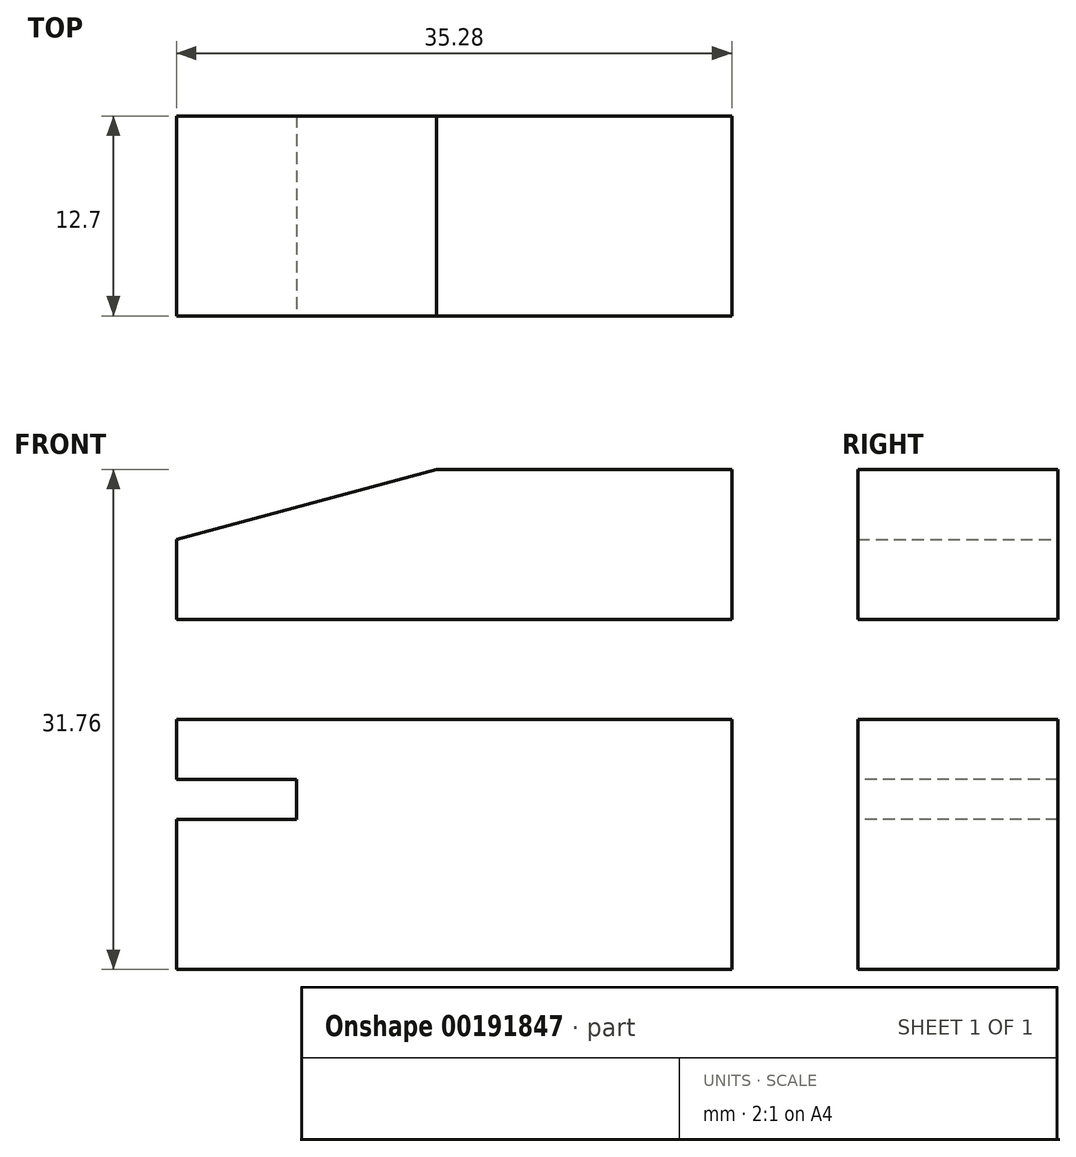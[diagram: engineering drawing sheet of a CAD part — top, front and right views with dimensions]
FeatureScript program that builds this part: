
annotation { "Feature Type Name" : "Feature", "Feature Type Description" : "" }
export const myFeature = defineFeature(function(context is Context, id is Id, definition is map)
    precondition{}
    {
        {
            var Q0;
            Q0=qCreatedBy(makeId("Front.planeOp"),FACE);
            var sketch = newSketch(context, id + "F0", { "sketchPlane" : qUnion([Q0])});
            skLineSegment(sketch, "E0.bottom", {"start": v(0, 0) * mm, "end": v(18.75, 0) * mm});
            skLineSegment(sketch, "E0.top", {"start": v(0, 9.52) * mm, "end": v(18.75, 9.52) * mm});
            skLineSegment(sketch, "E0.left", {"start": v(0, 0) * mm, "end": v(0, 9.52) * mm, "construction": true});
            skLineSegment(sketch, "E0.right", {"start": v(18.75, 0) * mm, "end": v(18.75, 9.52) * mm});
            skLineSegment(sketch, "E1", {"start": v(0, 9.52) * mm, "end": v(-16.53, 5.1) * mm});
            skLineSegment(sketch, "E2", {"start": v(-16.53, 5.1) * mm, "end": v(-16.53, 0) * mm});
            skLineSegment(sketch, "E3", {"start": v(-16.53, 0) * mm, "end": v(0, 0) * mm});
            skSolve(sketch);
        }
        {
            var Q0;
            Q0=makeQuery(id+"F0.imprint","IMPRINT",FACE,{"disambiguationData":[TD([[makeQuery(id+"F0.imprint","IMPRINT",EDGE,{"derivedFrom":sQuery(id+"F0.wireOp",EDGE,"E0.bottom")}),1.0]])]});
            extrude(context, id + "F1", {"entities" : qUnion([Q0]), "endBound" : BoundingType.SYMMETRIC, "depth" : 12.7 * mm});
        }
        {
            var Q0;
            Q0=qCreatedBy(makeId("Front.planeOp"),FACE);
            var sketch = newSketch(context, id + "F2", { "sketchPlane" : qUnion([Q0])});
            skLineSegment(sketch, "E4.bottom", {"start": v(18.75, -12.7) * mm, "end": v(-16.53, -12.7) * mm});
            skLineSegment(sketch, "E4.top", {"start": v(18.75, -22.23) * mm, "end": v(-16.53, -22.23) * mm});
            skLineSegment(sketch, "E4.left", {"start": v(18.75, -12.7) * mm, "end": v(18.75, -22.23) * mm});
            skLineSegment(sketch, "E4.right", {"start": v(-16.53, -12.7) * mm, "end": v(-16.53, -22.23) * mm});
            skSolve(sketch);
        }
        {
            var Q0;
            Q0=makeQuery(id+"F2.imprint","IMPRINT",FACE,{"disambiguationData":[TD([[makeQuery(id+"F2.imprint","IMPRINT",EDGE,{"derivedFrom":sQuery(id+"F2.wireOp",EDGE,"E4.bottom")}),1.0]])]});
            extrude(context, id + "F3", {"entities" : qUnion([Q0]), "endBound" : BoundingType.SYMMETRIC, "depth" : 12.7 * mm});
        }
        {
            var Q0;
            Q0=makeQuery(id+"F3.opExtrude","CAP_FACE",FACE,{"disambiguationData":[OSD([sQuery(id+"F2.wireOp",EDGE,"E4.bottom"),sQuery(id+"F2.wireOp",EDGE,"E4.top"),sQuery(id+"F2.wireOp",EDGE,"E4.left"),sQuery(id+"F2.wireOp",EDGE,"E4.right")])],"isStart":false});
            var sketch = newSketch(context, id + "F4", { "sketchPlane" : qUnion([Q0])});
            skLineSegment(sketch, "E5.bottom", {"start": v(18.75, -12.7) * mm, "end": v(-8.9, -12.7) * mm});
            skLineSegment(sketch, "E5.left", {"start": v(18.75, -12.7) * mm, "end": v(18.75, -10.16) * mm});
            skLineSegment(sketch, "E5.right", {"start": v(-8.9, -12.7) * mm, "end": v(-8.9, -10.16) * mm});
            skLineSegment(sketch, "E6.bottom", {"start": v(-16.53, -6.35) * mm, "end": v(18.75, -6.35) * mm});
            skLineSegment(sketch, "E6.top", {"start": v(-16.53, -10.16) * mm, "end": v(-8.9, -10.16) * mm});
            skLineSegment(sketch, "E6.left", {"start": v(-16.53, -6.35) * mm, "end": v(-16.53, -10.16) * mm});
            skLineSegment(sketch, "E6.right", {"start": v(18.75, -6.35) * mm, "end": v(18.75, -10.16) * mm});
            skSolve(sketch);
        }
        {
            var Q0;
            Q0=makeQuery(id+"F4.imprint","IMPRINT",FACE,{"disambiguationData":[TD([[makeQuery(id+"F4.imprint","IMPRINT",EDGE,{"derivedFrom":sQuery(id+"F4.wireOp",EDGE,"E5.bottom")}),-1.0]])]});
            var Q1;
            Q1=makeQuery(id+"F3.opExtrude","CAP_FACE",FACE,{"disambiguationData":[OSD([sQuery(id+"F2.wireOp",EDGE,"E4.bottom"),sQuery(id+"F2.wireOp",EDGE,"E4.top"),sQuery(id+"F2.wireOp",EDGE,"E4.left"),sQuery(id+"F2.wireOp",EDGE,"E4.right")])],"isStart":true});
            extrude(context, id + "F5", {"entities" : qUnion([Q0]), "operationType" : NewBodyOperationType.ADD, "endBound" : BoundingType.UP_TO_SURFACE, "oppositeDirection" : true, "endBoundEntityFace" : qUnion([Q1]), "depth" : 25.4 * mm});
        }
    });
